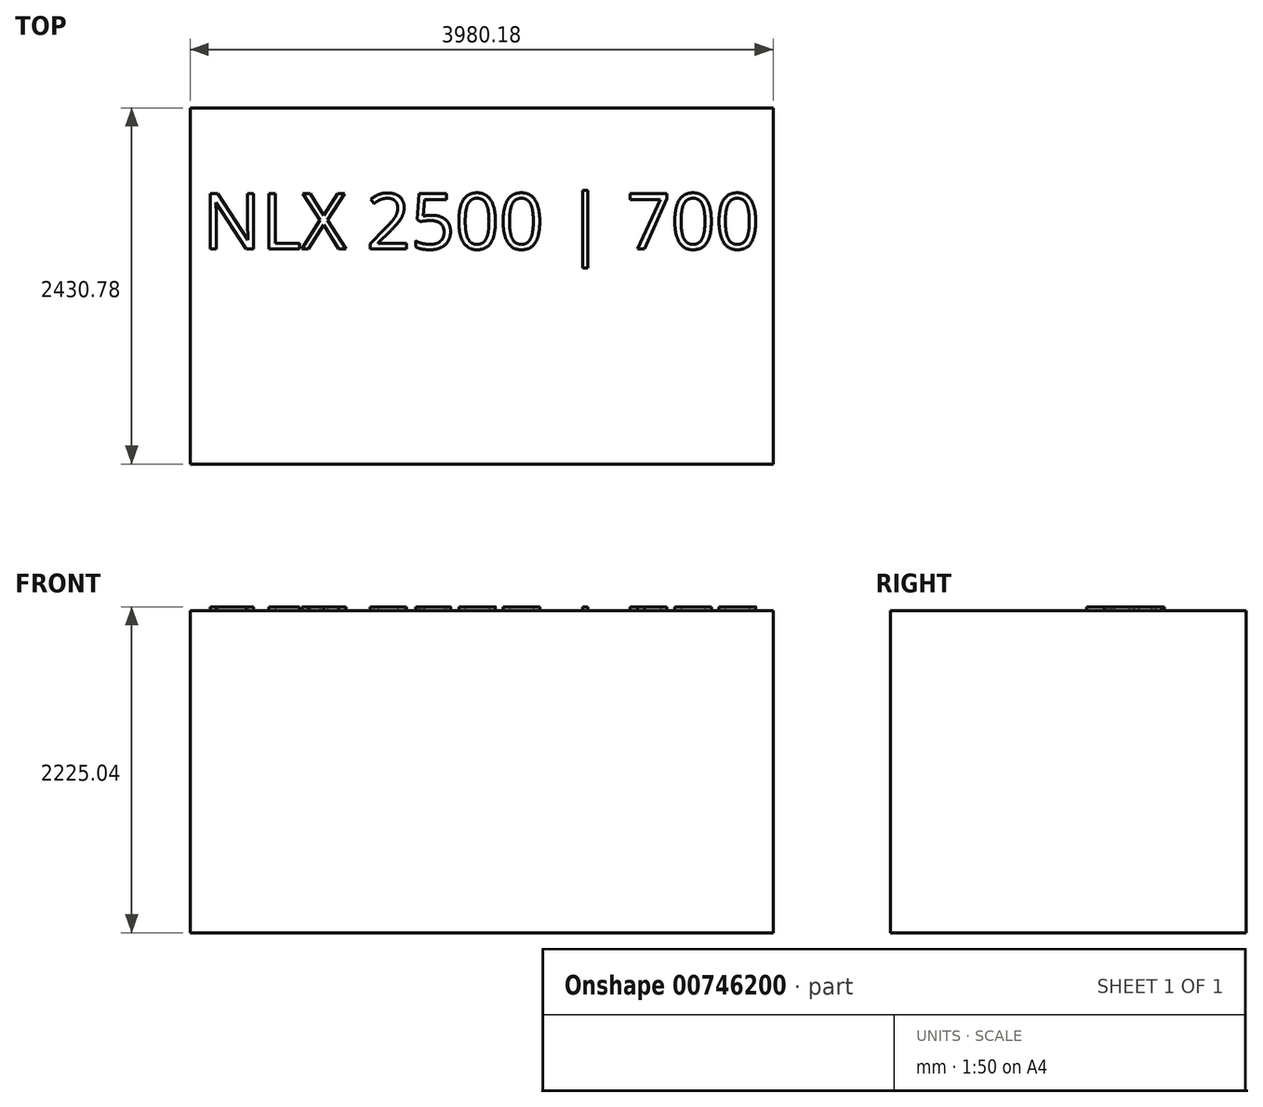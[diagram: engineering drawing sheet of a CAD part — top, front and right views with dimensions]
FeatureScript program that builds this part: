
annotation { "Feature Type Name" : "Feature", "Feature Type Description" : "" }
export const myFeature = defineFeature(function(context is Context, id is Id, definition is map)
    precondition{}
    {
        {
            var Q0;
            Q0=qCreatedBy(makeId("Top.planeOp"),FACE);
            var sketch = newSketch(context, id + "F0", { "sketchPlane" : qUnion([Q0])});
            skLineSegment(sketch, "E0.bottom", {"start": v(1990.1, -1215.4) * mm, "end": v(-1990.1, -1215.4) * mm});
            skLineSegment(sketch, "E0.top", {"start": v(1990.1, 1215.4) * mm, "end": v(-1990.1, 1215.39) * mm});
            skLineSegment(sketch, "E0.left", {"start": v(1990.1, -1215.39) * mm, "end": v(1990.1, 1215.4) * mm});
            skLineSegment(sketch, "E0.right", {"start": v(-1990.1, -1215.4) * mm, "end": v(-1990.1, 1215.39) * mm});
            skPoint(sketch, "E0.middle", {"position": v(0, 0) * mm});
            skSolve(sketch);
        }
        {
            var Q0;
            Q0 = qSketchRegion(id + "F0", true);
            extrude(context, id + "F1", {"entities" : qUnion([Q0]), "depth" : 2199.64 * mm, "offsetDistance" : 25.4 * mm});
        }
        {
            var Q0;
            Q0=makeQuery(id+"F1.opExtrude","CAP_FACE",FACE,{"disambiguationData":[OSD([sQuery(id+"F0.wireOp",EDGE,"E0.bottom"),sQuery(id+"F0.wireOp",EDGE,"E0.top"),sQuery(id+"F0.wireOp",EDGE,"E0.left"),sQuery(id+"F0.wireOp",EDGE,"E0.right")])],"isStart":false});
            var sketch = newSketch(context, id + "F2", { "sketchPlane" : qUnion([Q0])});
            skText(sketch, "E1", { "text": "NLX 2500 | 700\n", "fontName": "OpenSans-Regular.ttf"});
            const initialGuessF2  = {"E1": [-1.905, 0.25293, 1, 0, 0.38112]};
            skSetInitialGuess(sketch, initialGuessF2);
            skSolve(sketch);
        }
        {
            var Q0;
            Q0 = qSketchRegion(id + "F2", true);
            extrude(context, id + "F3", {"entities" : qUnion([Q0]), "operationType" : NewBodyOperationType.ADD, "depth" : 25.4 * mm, "offsetDistance" : 25.4 * mm});
        }
    });
